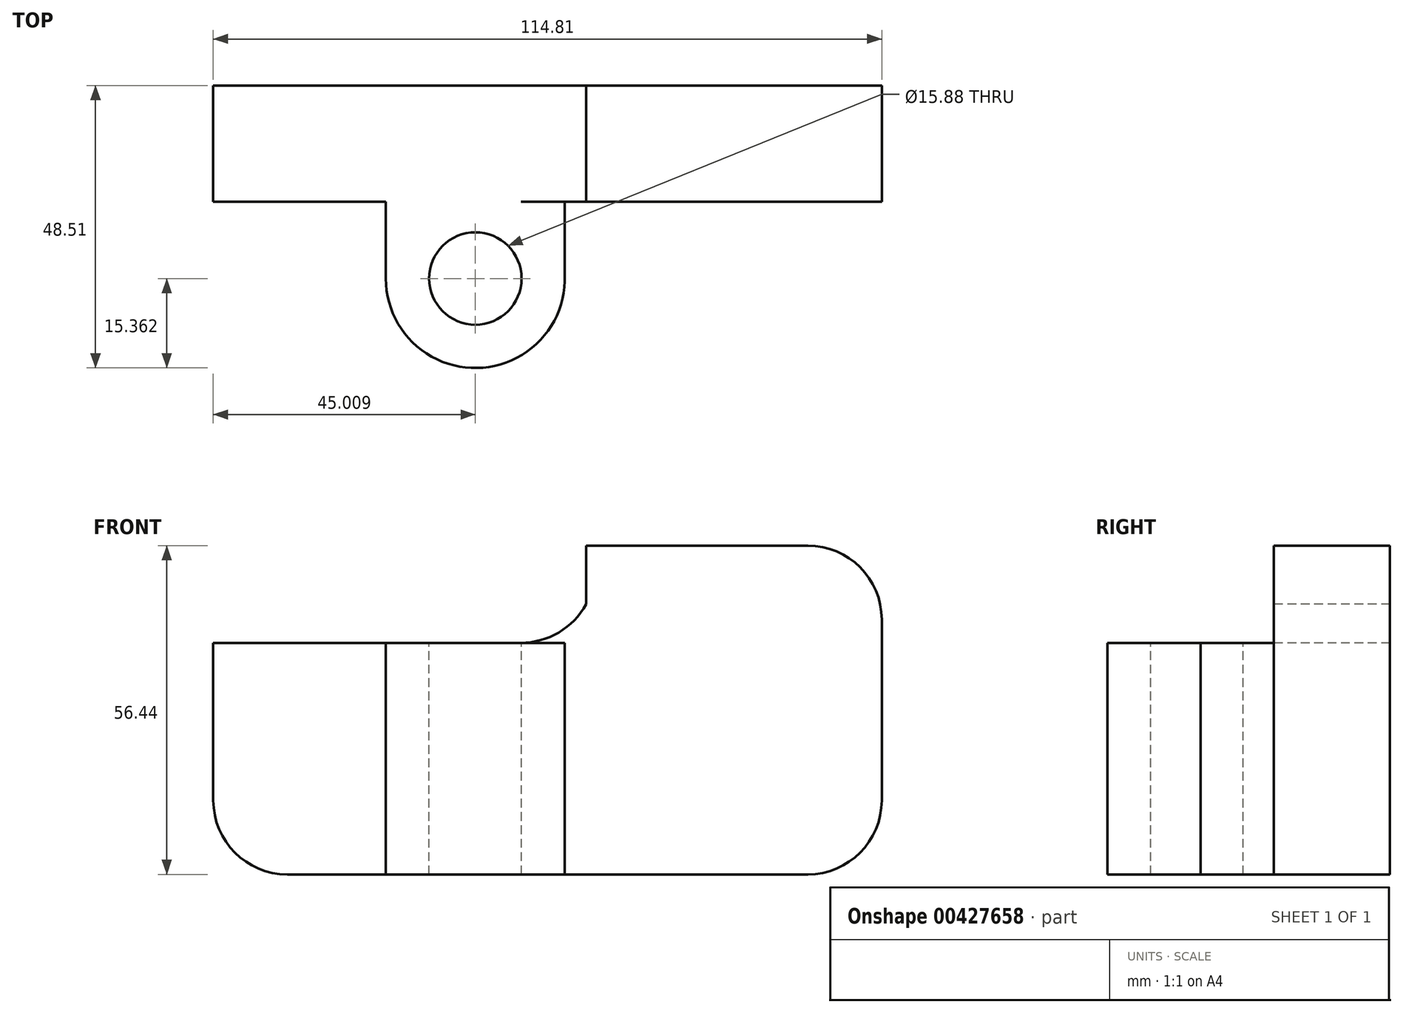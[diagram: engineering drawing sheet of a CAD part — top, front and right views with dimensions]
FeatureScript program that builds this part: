
annotation { "Feature Type Name" : "Feature", "Feature Type Description" : "" }
export const myFeature = defineFeature(function(context is Context, id is Id, definition is map)
    precondition{}
    {
        {
            var Q0;
            Q0=qCreatedBy(makeId("Top.planeOp"),FACE);
            var sketch = newSketch(context, id + "F0", { "sketchPlane" : qUnion([Q0])});
            skLineSegment(sketch, "E0.bottom", {"start": v(0, 0) * mm, "end": v(29.64, 0) * mm});
            skLineSegment(sketch, "E0.top", {"start": v(0, 19.94) * mm, "end": v(114.8, 19.94) * mm});
            skLineSegment(sketch, "E0.left", {"start": v(0, 0) * mm, "end": v(0, 19.94) * mm});
            skLineSegment(sketch, "E0.right", {"start": v(114.8, 0) * mm, "end": v(114.8, 19.94) * mm});
            skPoint(sketch, "E1", {"position": v(29.64, 0) * mm});
            skArc(sketch, "E2", {"start": v(29.64, -13.2) * mm, "mid": v(45.3, -28.57) * mm, "end": v(60.36, -12.61) * mm});
            skLineSegment(sketch, "E3", {"start": v(29.64, 0) * mm, "end": v(29.64, -13.2) * mm});
            skLineSegment(sketch, "E4", {"start": v(60.36, -12.61) * mm, "end": v(60.36, 0) * mm});
            skLineSegment(sketch, "E5.trimOffspring", {"start": v(60.36, 0) * mm, "end": v(114.8, 0) * mm});
            skSolve(sketch);
        }
        {
            var Q0;
            Q0 = qSketchRegion(id + "F0", true);
            extrude(context, id + "F1", {"entities" : qUnion([Q0]), "depth" : 56.44 * mm});
        }
        {
            var Q0;
            Q0=qCreatedBy(makeId("Front.planeOp"),FACE);
            var sketch = newSketch(context, id + "F2", { "sketchPlane" : qUnion([Q0])});
            skLineSegment(sketch, "E6", {"start": v(0, 39.75) * mm, "end": v(64, 39.75) * mm});
            skLineSegment(sketch, "E7", {"start": v(64, 39.75) * mm, "end": v(64, 56.44) * mm});
            skLineSegment(sketch, "E8", {"start": v(64, 56.44) * mm, "end": v(0, 56.44) * mm});
            skLineSegment(sketch, "E9", {"start": v(0, 56.44) * mm, "end": v(0, 39.75) * mm});
            skSolve(sketch);
        }
        {
            var Q0;
            Q0 = qSketchRegion(id + "F2", true);
            extrude(context, id + "F3", {"entities" : qUnion([Q0]), "operationType" : NewBodyOperationType.REMOVE, "oppositeDirection" : true, "depth" : 25.4 * mm, "hasSecondDirection" : true, "secondDirectionOppositeDirection" : false, "secondDirectionDepth" : 58.17 * mm});
        }
        {
            var Q0;
            Q0=makeQuery(id+"F1.opExtrude","CAP_EDGE",EDGE,{"disambiguationData":[OSD([sQuery(id+"F0.wireOp",EDGE,"E0.right")])],"isStart":false});
            var Q1;
            Q1=makeQuery(id+"F1.opExtrude","CAP_EDGE",EDGE,{"disambiguationData":[OSD([sQuery(id+"F0.wireOp",EDGE,"E0.right")])],"isStart":true});
            var Q2;
            Q2=makeQuery(id+"F3.boolean.opBoolean","COPY",EDGE,{"derivedFrom":makeQuery(id+"F3.opExtrude","SWEPT_EDGE",EDGE,{"disambiguationData":[OSD([sQuery(id+"F2.wireOp",EDGE,"E7"),sQuery(id+"F2.wireOp",EDGE,"E8")])]})});
            var Q3;
            Q3=makeQuery(id+"F3.boolean.opBoolean","COPY",EDGE,{"derivedFrom":makeQuery(id+"F3.opExtrude","SWEPT_EDGE",EDGE,{"disambiguationData":[OSD([sQuery(id+"F2.wireOp",EDGE,"E6"),sQuery(id+"F2.wireOp",EDGE,"E9")])]})});
            var Q4;
            Q4=makeQuery(id+"F1.opExtrude","CAP_EDGE",EDGE,{"disambiguationData":[OSD([sQuery(id+"F0.wireOp",EDGE,"E0.left")])],"isStart":true});
            fillet(context, id + "F4", {"entities" : qUnion([Q0, Q1, Q2, Q3, Q4]), "radius" : 12.7 * mm, "tangentPropagation" : true, "allowEdgeOverflow" : false});
        }
        {
            var Q0;
            Q0=qCreatedBy(makeId("Front.planeOp"),FACE);
            var sketch = newSketch(context, id + "F5", { "sketchPlane" : qUnion([Q0])});
            skLineSegment(sketch, "E10.0", {"start": v(60.38, 39.75) * mm, "end": v(52.85, 39.75) * mm});
            skLineSegment(sketch, "E11.0", {"start": v(64, 39.75) * mm, "end": v(60.36, 39.75) * mm});
            skLineSegment(sketch, "E12.0", {"start": v(64, 43.74) * mm, "end": v(64, 39.75) * mm});
            skArc(sketch, "E13.0", {"start": v(64.78, 48.1) * mm, "mid": v(64.2, 45.95) * mm, "end": v(64, 43.74) * mm});
            skArc(sketch, "E14", {"start": v(52.85, 39.75) * mm, "mid": v(60.13, 42.04) * mm, "end": v(64.78, 48.1) * mm});
            skPoint(sketch, "E14.first.point", {"position": v(52.85, 39.75) * mm});
            skPoint(sketch, "E14.second.point", {"position": v(64.78, 48.1) * mm});
            skPoint(sketch, "E14.third.point", {"position": v(41.14, 57.37) * mm});
            skPoint(sketch, "E15.orphan", {"position": v(29.64, 39.75) * mm});
            skPoint(sketch, "E16.orphan", {"position": v(76.7, 56.44) * mm});
            skSolve(sketch);
        }
        {
            var Q0;
            Q0 = qSketchRegion(id + "F5", true);
            var Q1;
            Q1=makeQuery(id+"F1.opExtrude","SWEPT_FACE",FACE,{"disambiguationData":[OSD([sQuery(id+"F0.wireOp",EDGE,"E0.top")])]});
            extrude(context, id + "F6", {"entities" : qUnion([Q0]), "operationType" : NewBodyOperationType.ADD, "endBound" : BoundingType.UP_TO_SURFACE, "oppositeDirection" : true, "endBoundEntityFace" : qUnion([Q1]), "depth" : 25.4 * mm});
        }
        {
            var Q0;
            Q0=makeQuery(id+"F3.boolean.opBoolean","COPY",FACE,{"derivedFrom":makeQuery(id+"F3.opExtrude","SWEPT_FACE",FACE,{"disambiguationData":[OSD([sQuery(id+"F2.wireOp",EDGE,"E6")])]})});
            var sketch = newSketch(context, id + "F7", { "sketchPlane" : qUnion([Q0])});
            skCircle(sketch, "E17", {"center": v(45, -13.2) * mm, "radius": 7.94 * mm});
            skSolve(sketch);
        }
        {
            var Q0;
            Q0 = qSketchRegion(id + "F7", true);
            var Q1;
            Q1=makeQuery(id+"F1.opExtrude","CAP_FACE",FACE,{"disambiguationData":[OSD([sQuery(id+"F0.wireOp",EDGE,"E0.bottom"),sQuery(id+"F0.wireOp",EDGE,"E0.top"),sQuery(id+"F0.wireOp",EDGE,"E0.left"),sQuery(id+"F0.wireOp",EDGE,"E0.right"),sQuery(id+"F0.wireOp",EDGE,"E2"),sQuery(id+"F0.wireOp",EDGE,"E3"),sQuery(id+"F0.wireOp",EDGE,"E4"),sQuery(id+"F0.wireOp",EDGE,"E5.trimOffspring")])],"isStart":true});
            extrude(context, id + "F8", {"entities" : qUnion([Q0]), "operationType" : NewBodyOperationType.REMOVE, "endBound" : BoundingType.UP_TO_SURFACE, "oppositeDirection" : true, "endBoundEntityFace" : qUnion([Q1]), "depth" : 25.4 * mm});
        }
    });
